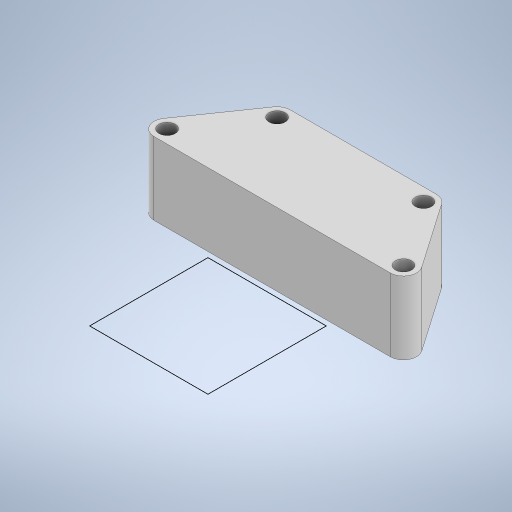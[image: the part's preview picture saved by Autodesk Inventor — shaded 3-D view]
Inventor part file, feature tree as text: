
AUTODESK INVENTOR PART (.ipt)
format: ipt  version: 2023 (Build 270158000, 158)  size: 239,104 bytes
history: native  units: in
note: dims shown in document units (in); Inventor stores cm internally (conversion verified against a paired STEP export)
features: sketch x2, extrude x1
ambient origin geometry x8: Origin, YZ Plane, XZ Plane, XY Plane, X Axis, Y Axis, Z Axis, Center Point
bodies: Solid1 (feature_tree)
feature tree (3):
  sketch  "Sketch1"  dims[d0=0.315in d1=0.315in]
  extrude  "Extrusion1"  Depth=0.315in
  sketch  "Sketch2"  dims[d2=0.315in d3=0.315in d4=0.874in d5=0.0in]
